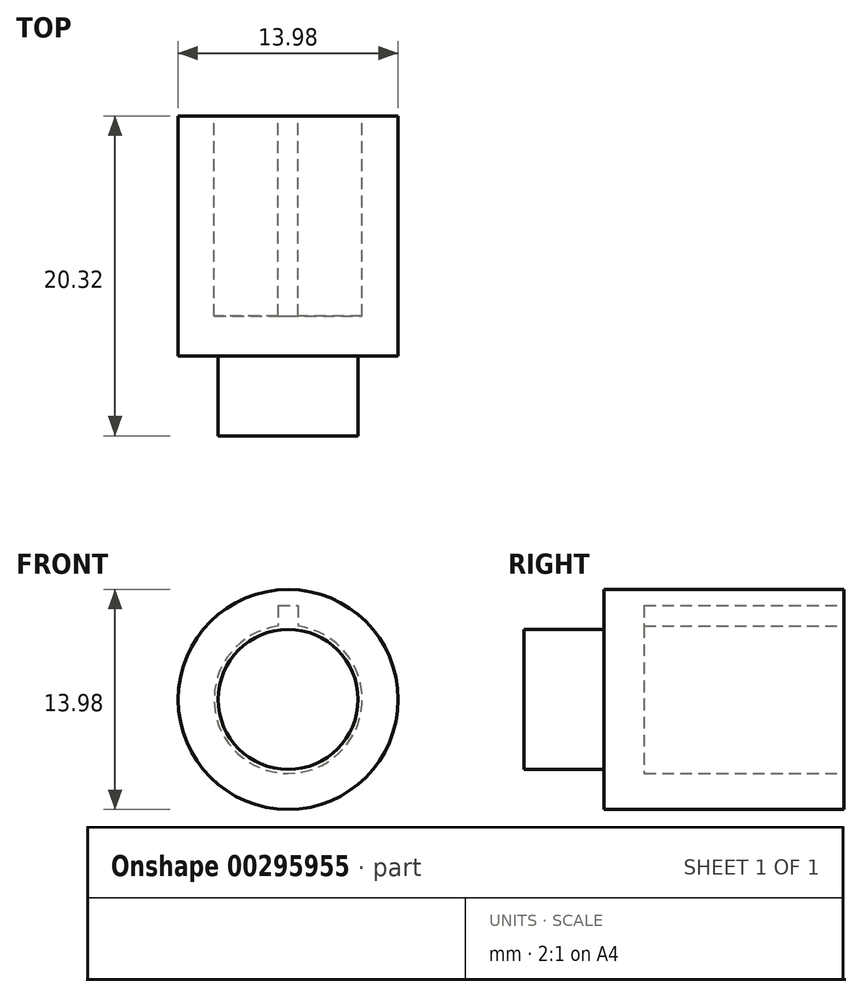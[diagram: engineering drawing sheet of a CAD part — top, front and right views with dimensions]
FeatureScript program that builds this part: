
annotation { "Feature Type Name" : "Feature", "Feature Type Description" : "" }
export const myFeature = defineFeature(function(context is Context, id is Id, definition is map)
    precondition{}
    {
        {
            var Q0;
            Q0=qCreatedBy(makeId("Front.planeOp"),FACE);
            var sketch = newSketch(context, id + "F0", { "sketchPlane" : qUnion([Q0])});
            skCircle(sketch, "E0", {"center": v(0, 0) * mm, "radius": 6.99 * mm});
            skCircle(sketch, "E1", {"center": v(0, 0) * mm, "radius": 4.7 * mm});
            skLineSegment(sketch, "E2", {"start": v(0, 4.7) * mm, "end": v(0, 5.97) * mm});
            skLineSegment(sketch, "E3", {"start": v(0, 5.97) * mm, "end": v(0.64, 5.97) * mm});
            skLineSegment(sketch, "E4", {"start": v(0.64, 5.97) * mm, "end": v(-0.64, 5.97) * mm});
            skLineSegment(sketch, "E5", {"start": v(-0.64, 5.97) * mm, "end": v(-0.64, 4.66) * mm});
            skLineSegment(sketch, "E6", {"start": v(0.64, 5.97) * mm, "end": v(0.64, 4.66) * mm});
            skSolve(sketch);
        }
        {
            var Q0;
            Q0 = qSketchRegion(id + "F0", true);
            extrude(context, id + "F1", {"entities" : qUnion([Q0]), "depth" : 12.7 * mm});
        }
        {
            var Q0;
            Q0=makeQuery(id+"F1.opExtrude","CAP_FACE",FACE,{"disambiguationData":[OSD([sQuery(id+"F0.wireOp",EDGE,"E0"),sQuery(id+"F0.wireOp",EDGE,"E1"),sQuery(id+"F0.wireOp",EDGE,"E4"),sQuery(id+"F0.wireOp",EDGE,"E5"),sQuery(id+"F0.wireOp",EDGE,"E6")])],"isStart":false});
            var sketch = newSketch(context, id + "F2", { "sketchPlane" : qUnion([Q0])});
            skCircle(sketch, "E7", {"center": v(0, 0) * mm, "radius": 6.99 * mm});
            skSolve(sketch);
        }
        {
            var Q0;
            Q0 = qSketchRegion(id + "F2", true);
            extrude(context, id + "F3", {"entities" : qUnion([Q0]), "operationType" : NewBodyOperationType.ADD, "depth" : 2.54 * mm});
        }
        {
            var Q0;
            Q0=makeQuery(id+"F3.opExtrude","CAP_FACE",FACE,{"disambiguationData":[OSD([sQuery(id+"F2.wireOp",EDGE,"E7")])],"isStart":false});
            var sketch = newSketch(context, id + "F4", { "sketchPlane" : qUnion([Q0])});
            skCircle(sketch, "E8", {"center": v(0, 0) * mm, "radius": 4.45 * mm});
            skSolve(sketch);
        }
        {
            var Q0;
            Q0 = qSketchRegion(id + "F4", true);
            var Q1;
            Q1=makeQuery(id+"F4.imprint","IMPRINT",FACE,{"disambiguationData":[TD([[makeQuery(id+"F4.imprint","IMPRINT",EDGE,{"derivedFrom":sQuery(id+"F4.wireOp",EDGE,"E8")}),1.0]])]});
            extrude(context, id + "F5", {"entities" : qUnion([Q0, Q1]), "operationType" : NewBodyOperationType.ADD, "depth" : 5.08 * mm});
        }
    });
